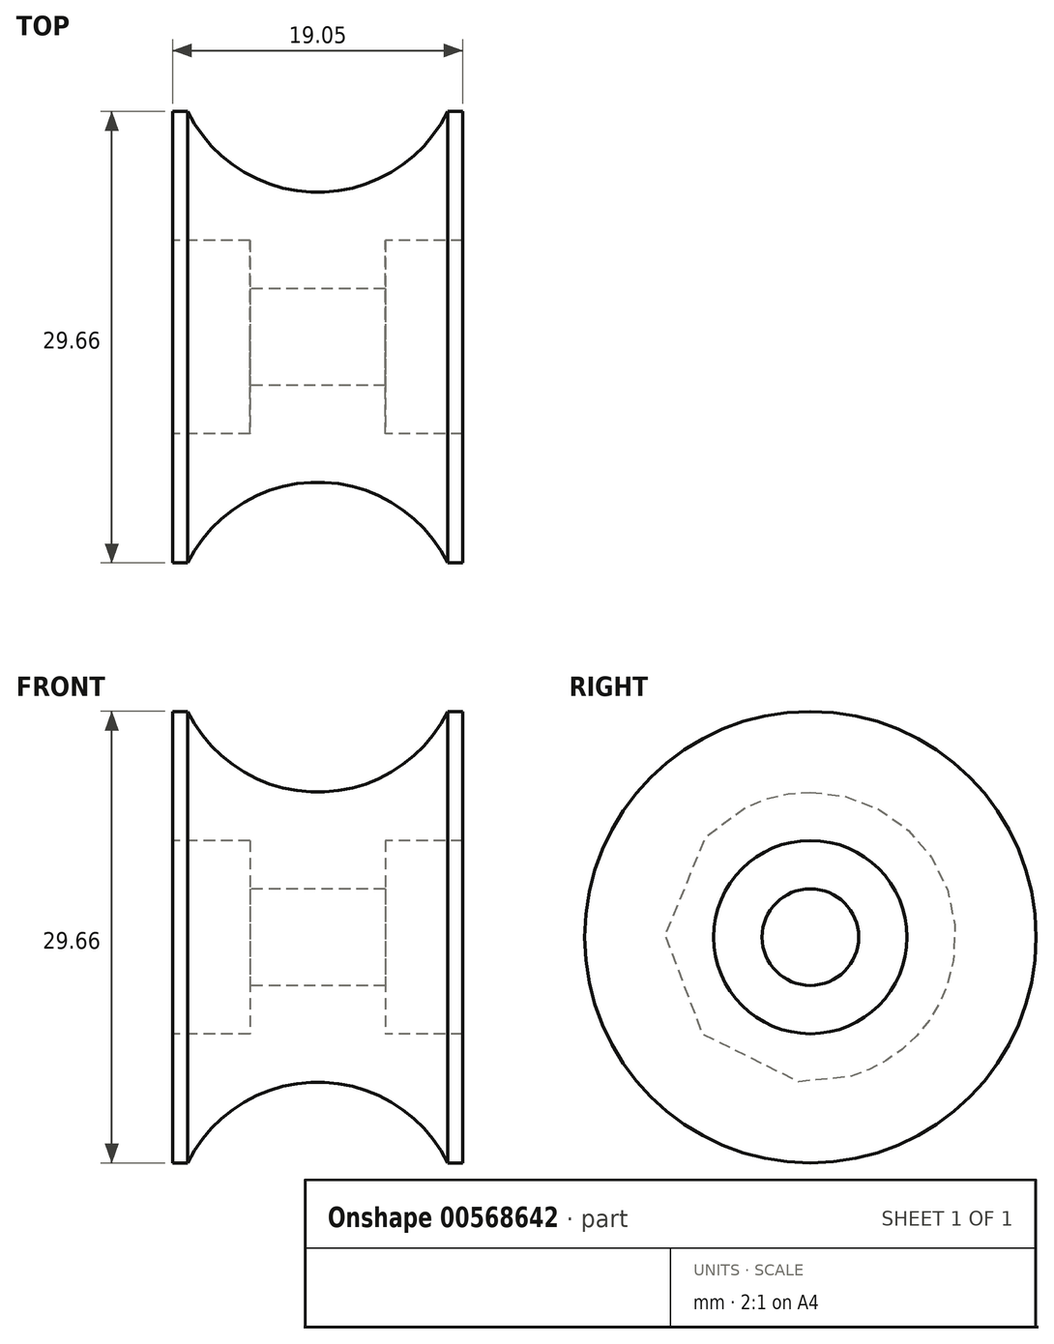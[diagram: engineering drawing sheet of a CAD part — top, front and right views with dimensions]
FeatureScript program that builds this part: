
annotation { "Feature Type Name" : "Feature", "Feature Type Description" : "" }
export const myFeature = defineFeature(function(context is Context, id is Id, definition is map)
    precondition{}
    {
        {
            var Q0;
            Q0=qCreatedBy(makeId("Front.planeOp"),FACE);
            var sketch = newSketch(context, id + "F0", { "sketchPlane" : qUnion([Q0])});
            skLineSegment(sketch, "E0", {"start": v(-19.85, 0) * mm, "end": v(61.06, 0) * mm, "construction": true});
            skLineSegment(sketch, "E1", {"start": v(9.29, 3.18) * mm, "end": v(18.18, 3.18) * mm});
            skLineSegment(sketch, "E2", {"start": v(18.18, 3.18) * mm, "end": v(18.18, 6.35) * mm});
            skLineSegment(sketch, "E3", {"start": v(18.18, 6.35) * mm, "end": v(23.26, 6.35) * mm});
            skLineSegment(sketch, "E4", {"start": v(23.26, 6.35) * mm, "end": v(23.26, 19.05) * mm});
            skLineSegment(sketch, "E5", {"start": v(9.29, 3.18) * mm, "end": v(9.29, 6.35) * mm});
            skLineSegment(sketch, "E6", {"start": v(9.29, 6.35) * mm, "end": v(4.2, 6.35) * mm});
            skLineSegment(sketch, "E7", {"start": v(4.2, 6.35) * mm, "end": v(4.2, 19.05) * mm});
            skPoint(sketch, "E8.centerSnap0", {"position": v(13.73, 3.18) * mm});
            skArc(sketch, "E9", {"start": v(4.2, 19.05) * mm, "mid": v(13.73, 9.53) * mm, "end": v(23.26, 19.05) * mm});
            skLineSegment(sketch, "E10", {"start": v(4.2, 14.83) * mm, "end": v(5.2, 14.83) * mm});
            skLineSegment(sketch, "E11", {"start": v(23.26, 14.83) * mm, "end": v(22.27, 14.83) * mm});
            skSolve(sketch);
        }
        {
            var Q0;
            Q0=makeQuery(id+"F0.imprint","IMPRINT",FACE,{"disambiguationData":[TD([[makeQuery(id+"F0.imprint","IMPRINT",EDGE,{"derivedFrom":sQuery(id+"F0.wireOp",EDGE,"E1")}),1.0]])]});
            var Q1;
            Q1=sQuery(id+"F0.wireOp",EDGE,"E0");
            revolve(context, id + "F1", {"entities" : qUnion([Q0]), "axis" : qUnion([Q1]), "revolveType" : RevolveType.FULL});
        }
    });
